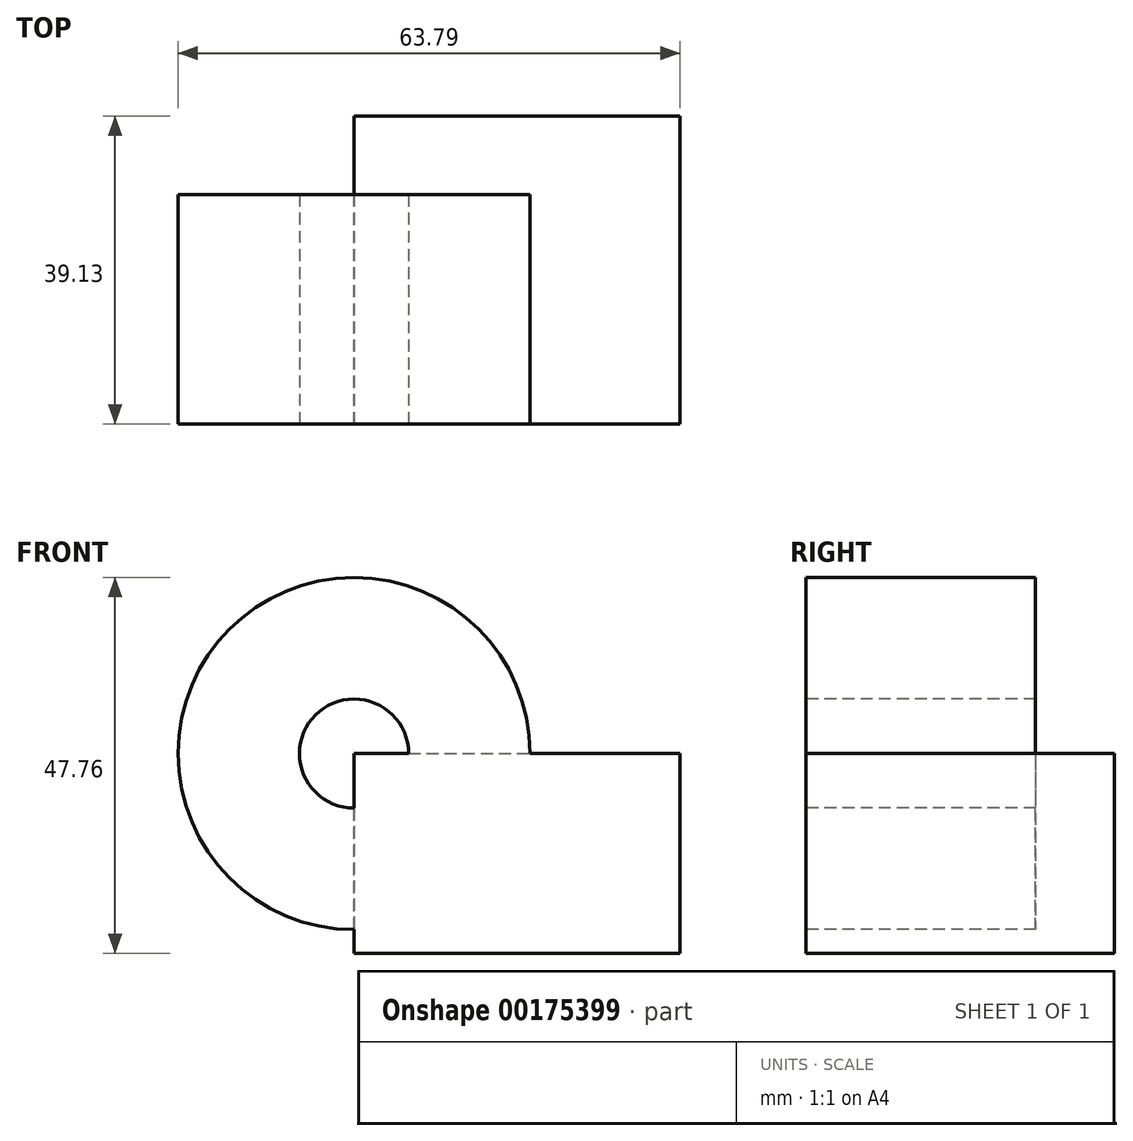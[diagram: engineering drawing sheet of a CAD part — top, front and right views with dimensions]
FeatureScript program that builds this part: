
annotation { "Feature Type Name" : "Feature", "Feature Type Description" : "" }
export const myFeature = defineFeature(function(context is Context, id is Id, definition is map)
    precondition{}
    {
        {
            var Q0;
            Q0=qCreatedBy(makeId("Top.planeOp"),FACE);
            var sketch = newSketch(context, id + "F0", { "sketchPlane" : qUnion([Q0])});
            skLineSegment(sketch, "E0.bottom", {"start": v(0, 0) * mm, "end": v(41.43, 0) * mm});
            skLineSegment(sketch, "E0.top", {"start": v(0, 39.13) * mm, "end": v(41.43, 39.13) * mm});
            skLineSegment(sketch, "E0.left", {"start": v(0, 0) * mm, "end": v(0, 39.13) * mm});
            skLineSegment(sketch, "E0.right", {"start": v(41.43, 0) * mm, "end": v(41.43, 39.13) * mm});
            skSolve(sketch);
        }
        {
            var Q0;
            Q0 = qSketchRegion(id + "F0", true);
            extrude(context, id + "F1", {"entities" : qUnion([Q0]), "depth" : 25.4 * mm});
        }
        {
            var Q0;
            Q0=makeQuery(id+"F1.opExtrude","CAP_FACE",FACE,{"disambiguationData":[OSD([sQuery(id+"F0.wireOp",EDGE,"E0.bottom"),sQuery(id+"F0.wireOp",EDGE,"E0.top"),sQuery(id+"F0.wireOp",EDGE,"E0.left"),sQuery(id+"F0.wireOp",EDGE,"E0.right")])],"isStart":false});
            var sketch = newSketch(context, id + "F2", { "sketchPlane" : qUnion([Q0])});
            skLineSegment(sketch, "E1.bottom", {"start": v(6.93, 0) * mm, "end": v(22.36, 0) * mm});
            skLineSegment(sketch, "E1.top", {"start": v(6.93, 29.13) * mm, "end": v(22.36, 29.13) * mm});
            skLineSegment(sketch, "E1.left", {"start": v(6.93, 0) * mm, "end": v(6.93, 29.13) * mm});
            skLineSegment(sketch, "E1.right", {"start": v(22.36, 0) * mm, "end": v(22.36, 29.13) * mm});
            skSolve(sketch);
        }
        {
            var Q0;
            Q0=makeQuery(id+"F2.imprint","IMPRINT",FACE,{"disambiguationData":[TD([[makeQuery(id+"F2.imprint","IMPRINT",EDGE,{"derivedFrom":sQuery(id+"F2.wireOp",EDGE,"E1.bottom")}),1.0]])]});
            var Q1;
            Q1=makeQuery(id+"F1.opExtrude","CAP_EDGE",EDGE,{"disambiguationData":[OSD([sQuery(id+"F0.wireOp",EDGE,"E0.left")])],"isStart":false});
            revolve(context, id + "F3", {"operationType" : NewBodyOperationType.ADD, "entities" : qUnion([Q0]), "axis" : qUnion([Q1]), "revolveType" : RevolveType.FULL});
        }
    });
